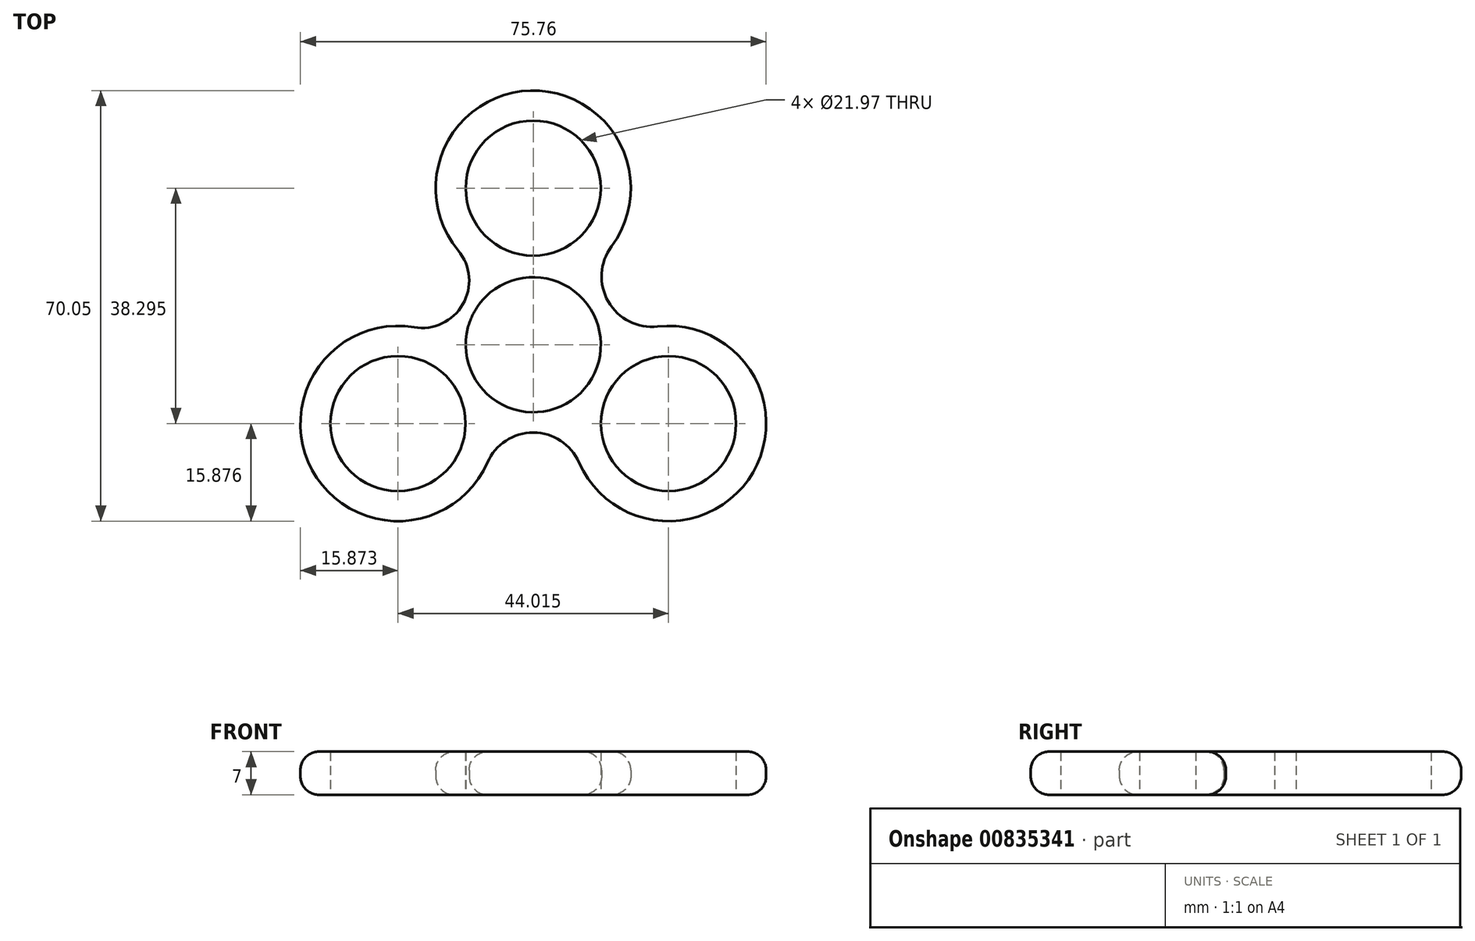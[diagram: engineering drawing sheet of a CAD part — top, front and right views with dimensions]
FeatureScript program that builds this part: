
annotation { "Feature Type Name" : "Feature", "Feature Type Description" : "" }
export const myFeature = defineFeature(function(context is Context, id is Id, definition is map)
    precondition{}
    {
        {
            var Q0;
            Q0=qCreatedBy(makeId("Top.planeOp"),FACE);
            var sketch = newSketch(context, id + "F0", { "sketchPlane" : qUnion([Q0])});
            skCircle(sketch, "E0", {"center": v(0, 0) * mm, "radius": 10.99 * mm});
            skCircle(sketch, "E1", {"center": v(0, 0) * mm, "radius": 25.47 * mm, "construction": true});
            skCircle(sketch, "E2", {"center": v(0, 25.47) * mm, "radius": 10.99 * mm});
            skCircle(sketch, "E3", {"center": v(-22, -12.82) * mm, "radius": 10.99 * mm});
            skCircle(sketch, "E4", {"center": v(22, -12.82) * mm, "radius": 10.99 * mm});
            skLineSegment(sketch, "E5", {"start": v(-22, -12.82) * mm, "end": v(-11.02, -12.82) * mm, "construction": true});
            skLineSegment(sketch, "E6", {"start": v(0, 25.47) * mm, "end": v(-5.47, 15.95) * mm, "construction": true});
            skLineSegment(sketch, "E7", {"start": v(22, -12.82) * mm, "end": v(16.53, -3.3) * mm, "construction": true});
            skLineSegment(sketch, "E8.bottom", {"start": v(-57.15, 57.15) * mm, "end": v(57.15, 57.15) * mm, "construction": true});
            skLineSegment(sketch, "E8.top", {"start": v(-57.15, -57.15) * mm, "end": v(57.15, -57.15) * mm, "construction": true});
            skLineSegment(sketch, "E8.left", {"start": v(-57.15, 57.15) * mm, "end": v(-57.15, -57.15) * mm, "construction": true});
            skLineSegment(sketch, "E8.right", {"start": v(57.15, 57.15) * mm, "end": v(57.15, -57.15) * mm, "construction": true});
            skPoint(sketch, "E9", {"position": v(-57.15, 0) * mm});
            skPoint(sketch, "E10", {"position": v(0, 57.15) * mm});
            skArc(sketch, "E11", {"start": v(12.74, 16) * mm, "mid": v(-0.43, 41.34) * mm, "end": v(-12.2, 15.32) * mm});
            skArc(sketch, "E12", {"start": v(7.45, -19.15) * mm, "mid": v(35.75, -20.77) * mm, "end": v(20.23, 2.95) * mm});
            skArc(sketch, "E13", {"start": v(-19.38, 2.83) * mm, "mid": v(-35.96, -20.4) * mm, "end": v(-7.45, -19.15) * mm});
            skLineSegment(sketch, "E14.trimOffspring", {"start": v(-16.53, -3.3) * mm, "end": v(-22, -12.82) * mm, "construction": true});
            skLineSegment(sketch, "E15.trimOffspring", {"start": v(5.47, 15.95) * mm, "end": v(0, 25.47) * mm, "construction": true});
            skLineSegment(sketch, "E16.trimOffspring", {"start": v(11.02, -12.82) * mm, "end": v(22, -12.82) * mm, "construction": true});
            skPoint(sketch, "E17.end.orphan", {"position": v(9.06, 11.07) * mm});
            skPoint(sketch, "E18.orphan", {"position": v(9.06, 12.44) * mm});
            skArc(sketch, "E19", {"start": v(12.74, 16) * mm, "mid": v(12.2, 7.02) * mm, "end": v(20.23, 2.95) * mm});
            skPoint(sketch, "E20.visualSharp", {"position": v(-12.63, 15.86) * mm});
            skArc(sketch, "E21", {"start": v(-19.38, 2.83) * mm, "mid": v(-11.45, 6.58) * mm, "end": v(-12.2, 15.32) * mm});
            skArc(sketch, "E22", {"start": v(7.45, -19.15) * mm, "mid": v(0, -14.27) * mm, "end": v(-7.45, -19.15) * mm});
            skSolve(sketch);
        }
        {
            var Q0;
            Q0=makeQuery(id+"F0.imprint","IMPRINT",FACE,{"disambiguationData":[TD([[makeQuery(id+"F0.imprint","IMPRINT",EDGE,{"derivedFrom":sQuery(id+"F0.wireOp",EDGE,"E0")}),-1.0]])]});
            extrude(context, id + "F1", {"entities" : qUnion([Q0]), "depth" : 7 * mm, "offsetDistance" : 25.4 * mm});
        }
        {
            var Q0;
            Q0=makeQuery(id+"F1.opExtrude","CAP_EDGE",EDGE,{"disambiguationData":[OSD([sQuery(id+"F0.wireOp",EDGE,"E11")])],"isStart":false});
            var Q1;
            Q1=makeQuery(id+"F1.opExtrude","CAP_EDGE",EDGE,{"disambiguationData":[OSD([sQuery(id+"F0.wireOp",EDGE,"ORf32fNm-emA0-bikx-w8Zo-7VFVjEIhLGI0")])],"isStart":false});
            var Q2;
            Q2=makeQuery(id+"F1.opExtrude","CAP_EDGE",EDGE,{"disambiguationData":[OSD([sQuery(id+"F0.wireOp",EDGE,"fN55ttd0-f0GO-9BtL-sMbP-4jCXobsnnuQ5")])],"isStart":false});
            var Q3;
            Q3=makeQuery(id+"F1.opExtrude","CAP_EDGE",EDGE,{"disambiguationData":[OSD([sQuery(id+"F0.wireOp",EDGE,"RcQCgj6x-oDMk-RVwQ-P6yw-V12OFnsf9GKq")])],"isStart":false});
            var Q4;
            Q4=makeQuery(id+"F1.opExtrude","CAP_EDGE",EDGE,{"disambiguationData":[OSD([sQuery(id+"F0.wireOp",EDGE,"E13")])],"isStart":false});
            var Q5;
            Q5=makeQuery(id+"F1.opExtrude","CAP_EDGE",EDGE,{"disambiguationData":[OSD([sQuery(id+"F0.wireOp",EDGE,"ZE9QFr35-ArW0-3ib2-GfmY-b7PQa5dmHP2M")])],"isStart":false});
            var Q6;
            Q6=makeQuery(id+"F1.opExtrude","CAP_EDGE",EDGE,{"disambiguationData":[OSD([sQuery(id+"F0.wireOp",EDGE,"14e375ba-32c4-4195-9f6d-e4428f817aa9.trimOffspring")])],"isStart":false});
            var Q7;
            Q7=makeQuery(id+"F1.opExtrude","CAP_EDGE",EDGE,{"disambiguationData":[OSD([sQuery(id+"F0.wireOp",EDGE,"LZRCFfsA-1dFh-KL0r-nv1u-hTn9DSQMTJ32")])],"isStart":false});
            var Q8;
            Q8=makeQuery(id+"F1.opExtrude","CAP_EDGE",EDGE,{"disambiguationData":[OSD([sQuery(id+"F0.wireOp",EDGE,"E12")])],"isStart":false});
            var Q9;
            Q9=makeQuery(id+"F1.opExtrude","CAP_EDGE",EDGE,{"disambiguationData":[OSD([sQuery(id+"F0.wireOp",EDGE,"s3swRYTc-Yoj9-jtKb-jrqV-ckIsDFl1wpzs")])],"isStart":false});
            var Q10;
            Q10=makeQuery(id+"F1.opExtrude","CAP_EDGE",EDGE,{"disambiguationData":[OSD([sQuery(id+"F0.wireOp",EDGE,"8aef53c4-0253-40b3-8aa8-6842bcded28d.trimOffspring")])],"isStart":false});
            var Q11;
            Q11=makeQuery(id+"F1.opExtrude","CAP_EDGE",EDGE,{"disambiguationData":[OSD([sQuery(id+"F0.wireOp",EDGE,"pG0xs2JO-FNxe-vMp4-gf7X-NJSgpntZNAZb")])],"isStart":false});
            fillet(context, id + "F2", {"entities" : qUnion([Q0, Q1, Q2, Q3, Q4, Q5, Q6, Q7, Q8, Q9, Q10, Q11]), "radius" : 3 * mm, "tangentPropagation" : true, "allowEdgeOverflow" : false});
        }
        {
            var Q0;
            Q0=makeQuery(id+"F1.opExtrude","CAP_EDGE",EDGE,{"disambiguationData":[OSD([sQuery(id+"F0.wireOp",EDGE,"E11")])],"isStart":true});
            var Q1;
            Q1=makeQuery(id+"F1.opExtrude","CAP_EDGE",EDGE,{"disambiguationData":[OSD([sQuery(id+"F0.wireOp",EDGE,"pG0xs2JO-FNxe-vMp4-gf7X-NJSgpntZNAZb")])],"isStart":true});
            var Q2;
            Q2=makeQuery(id+"F1.opExtrude","CAP_EDGE",EDGE,{"disambiguationData":[OSD([sQuery(id+"F0.wireOp",EDGE,"8aef53c4-0253-40b3-8aa8-6842bcded28d.trimOffspring")])],"isStart":true});
            var Q3;
            Q3=makeQuery(id+"F1.opExtrude","CAP_EDGE",EDGE,{"disambiguationData":[OSD([sQuery(id+"F0.wireOp",EDGE,"s3swRYTc-Yoj9-jtKb-jrqV-ckIsDFl1wpzs")])],"isStart":true});
            var Q4;
            Q4=makeQuery(id+"F1.opExtrude","CAP_EDGE",EDGE,{"disambiguationData":[OSD([sQuery(id+"F0.wireOp",EDGE,"E12")])],"isStart":true});
            var Q5;
            Q5=makeQuery(id+"F1.opExtrude","CAP_EDGE",EDGE,{"disambiguationData":[OSD([sQuery(id+"F0.wireOp",EDGE,"LZRCFfsA-1dFh-KL0r-nv1u-hTn9DSQMTJ32")])],"isStart":true});
            var Q6;
            Q6=makeQuery(id+"F1.opExtrude","CAP_EDGE",EDGE,{"disambiguationData":[OSD([sQuery(id+"F0.wireOp",EDGE,"14e375ba-32c4-4195-9f6d-e4428f817aa9.trimOffspring")])],"isStart":true});
            var Q7;
            Q7=makeQuery(id+"F1.opExtrude","CAP_EDGE",EDGE,{"disambiguationData":[OSD([sQuery(id+"F0.wireOp",EDGE,"ZE9QFr35-ArW0-3ib2-GfmY-b7PQa5dmHP2M")])],"isStart":true});
            var Q8;
            Q8=makeQuery(id+"F1.opExtrude","CAP_EDGE",EDGE,{"disambiguationData":[OSD([sQuery(id+"F0.wireOp",EDGE,"E13")])],"isStart":true});
            var Q9;
            Q9=makeQuery(id+"F1.opExtrude","CAP_EDGE",EDGE,{"disambiguationData":[OSD([sQuery(id+"F0.wireOp",EDGE,"RcQCgj6x-oDMk-RVwQ-P6yw-V12OFnsf9GKq")])],"isStart":true});
            var Q10;
            Q10=makeQuery(id+"F1.opExtrude","CAP_EDGE",EDGE,{"disambiguationData":[OSD([sQuery(id+"F0.wireOp",EDGE,"fN55ttd0-f0GO-9BtL-sMbP-4jCXobsnnuQ5")])],"isStart":true});
            var Q11;
            Q11=makeQuery(id+"F1.opExtrude","CAP_EDGE",EDGE,{"disambiguationData":[OSD([sQuery(id+"F0.wireOp",EDGE,"ORf32fNm-emA0-bikx-w8Zo-7VFVjEIhLGI0")])],"isStart":true});
            fillet(context, id + "F3", {"entities" : qUnion([Q0, Q1, Q2, Q3, Q4, Q5, Q6, Q7, Q8, Q9, Q10, Q11]), "radius" : 3 * mm, "tangentPropagation" : true, "allowEdgeOverflow" : false});
        }
    });
